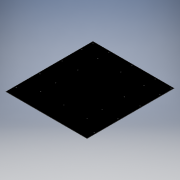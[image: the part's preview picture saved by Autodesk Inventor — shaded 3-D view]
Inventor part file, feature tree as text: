
AUTODESK INVENTOR PART (.ipt)
format: ipt  version: 2017.3 (Build 213256000, 256)  size: 150,528 bytes
history: native  units: mm
features: sheet_metal_op x1, sketch x1, other x1
ambient origin geometry x8: Origin, YZ Plane, XZ Plane, XY Plane, X Axis, Y Axis, Z Axis, Center Point
bodies: Body1 (feature_tree)
feature tree (3):
  sheet_metal_op  "Face5"
  sketch  "Sketch1"  dims[d0=513.0mm d1=550.0mm d2=10.0mm d3=10.0mm d4=10.0mm d5=110.0mm d6=80.0mm d7=110.0mm d8=110.0mm d9=70.0mm d10=55.0mm d11=4.2mm d12=1.5mm d13=1.5mm d16=1.5mm d19=1.5mm d20=1.5mm]
  other  "Plate5"
